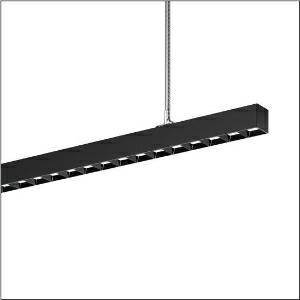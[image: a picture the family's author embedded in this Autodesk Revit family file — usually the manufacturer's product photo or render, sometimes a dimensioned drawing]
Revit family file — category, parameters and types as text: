
# Revit family: silica_r__21_51mx32tctdb_2a66
name_source: partatom
category: Lighting Fixtures
units: mm (PartAtom-declared; Revit-internal decimal feet)

## family parameters
Cut with Voids When Loaded = No
Host = Face
Light Source = No
Part Type = Normal
Room Calculation Point = No
Round Connector Dimension = Use Diameter
Shared = No

## types (1)
- --- (1 x LED, 15540 lm, 133.6 W, 6500K)
    Apparent Load = 134 VA
    CIE Flux Codes = 84 99 100 60 100
    Color Rendering = 80
    Color Temperature = 6500K
    Default Elevation = 1800 mm
    Description = Silica® 21, office luminaire, primary light control with darklight reflector, of PMMA, black, CAT 2 (L<= 3000cd/m²), light emission: direct/indirect distribution, primary light characteristic: symmetric, installation type: suspended mounting, LED, rated luminous flux: 15.540lm, luminous efficacy: 111lm/W, light colour: 8tw, colour temperature: 2700..6500K, control gear: ECG DALI, with terminal, 3+2-pole, max. 2.5mm², mains connection: 220..240V, AC, 50/60Hz, rated input power: 140.3W, luminaire housing, of aluminium, jet black (RAL 9005), length: 3.004mm, width: 53mm, height: 53mm, protection rating (complete): IP20, insulation class (complete): insulation class I (protective earthing), certification: CE, permissible operating ambient temperature: 0..+35°C, standard: EN 50419, packaging unit: 1 piece
    Height = 53 mm
    Lamp = 1 x LED
    Lamp Light Flux = 15540 lm
    Lamp Power = 133.6 W
    Lamp count = 1
    Length = 3004 mm
    Luminous efficacy = 116 lm/W
    Manufacturer = Siteco
    ModVariant = No
    Model = 51MX32TCTDB
    Mounting Place = Ceiling
    Mounting Type = Pendant
    Number of Poles = 1
    OnlyDefault = Yes
    Power Factor = 1
    Product Name = Silica® 21
    Product group = office luminaire | ceiling pendant
    ProductGroupID = 905
    Protection Class = Protection class I
    Protection Degree = IP 20
    RLX_Detail_Level = 1
    RlxData = <blob elided: 63305 chars, md5=02d8f620>
    Socket = socket
    Standby Power = 0 W
    System Light Flux = 15540 lm
    System Power = 134 W
    Type Comments = individual setting
    Type Image = l_1251718.jpg
    URL = http://relux.com
    VarID = @adj_046023
    Voltage = 0 V
    Weight = 0.00 kg
    Width = 53 mm

## geometry (parser evidence)
native form markers: Blend x4, Sweep x11
no freeform markers — native parametric forms only
